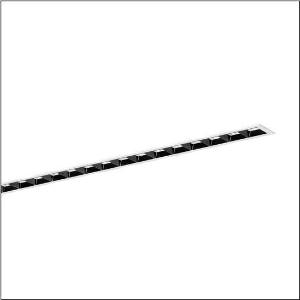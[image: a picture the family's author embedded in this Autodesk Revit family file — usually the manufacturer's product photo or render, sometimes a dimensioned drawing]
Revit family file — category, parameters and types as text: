
# Revit family: silica_r__21_51mx11tat4w_b1e5
name_source: partatom
category: Lighting Fixtures
units: mm (PartAtom-declared; Revit-internal decimal feet)

## family parameters
Cut with Voids When Loaded = No
Host = Face
Light Source = No
Part Type = Normal
Room Calculation Point = No
Round Connector Dimension = Use Diameter
Shared = No

## types (1)
- --- (1 x LED, 3720 lm, 32.2 W, 6500K)
    Apparent Load = 32 VA
    CIE Flux Codes = 85 99 100 100 100
    Color Rendering = 80
    Color Temperature = 6500K
    Default Elevation = 1800 mm
    Description = Silica® 21, office luminaire, primary light control with darklight reflector, of PMMA, black, CAT 2 (L<= 3000cd/m²), light emission: direct distribution, primary light characteristic: symmetric, installation type: recessed, LED, rated luminous flux: 3.720lm, luminous efficacy: 110lm/W, light colour: 8tw, colour temperature: 2700..6500K, with terminal, 3+2-pole, max. 2.5mm², mains connection: 220..240V, AC, 50/60Hz, rated input power: 33.8W, luminaire housing, of aluminium, traffic white (RAL 9016), length: 1.228mm, width: 79mm, height: 53mm, protection rating (complete): IP20, insulation class (complete): insulation class I (protective earthing), certification: CE, permissible operating ambient temperature: 0..+35°C, standard: EN 50419, packaging unit: 1 piece
    Height = 0 mm  [stored 0 ft]
    Lamp = 1 x LED
    Lamp Light Flux = 3720 lm
    Lamp Power = 32.2 W
    Lamp count = 1
    Length = 1227 mm
    Luminous efficacy = 116 lm/W
    Manufacturer = Siteco
    ModVariant = No
    Model = 51MX11TAT4W
    Mounting Place = Ceiling
    Mounting Type = Recessed
    Number of Poles = 1
    OnlyDefault = Yes
    Power Factor = 1
    Product Name = Silica® 21
    Product group = office luminaire | ceiling recessed
    ProductGroupID = 401
    Protection Class = Protection class I
    Protection Degree = IP 20
    RLX_Detail_Level = 1
    RLX_Emergency_Light_Flux = 0 lm
    RLX_Emergency_Type = 0
    RLX_Emergency_Type_DB = No
    RlxData = <blob elided: 35729 chars, md5=b44a84ca>
    Socket = socket
    Standby Power = 0 W
    System Light Flux = 3720 lm
    System Power = 32 W
    Type Comments = individual setting
    Type Image = l_1297791.jpg
    URL = http://relux.com
    VarID = @adj_071431
    Voltage = 0 V
    Weight = 0.00 kg
    Width = 79 mm

note: [stored X ft] marks values corroborated as IEEE doubles in the binary element streams (Revit-internal decimal feet)

## geometry (parser evidence)
native form markers: Blend x4, Sweep x10
no freeform markers — native parametric forms only
